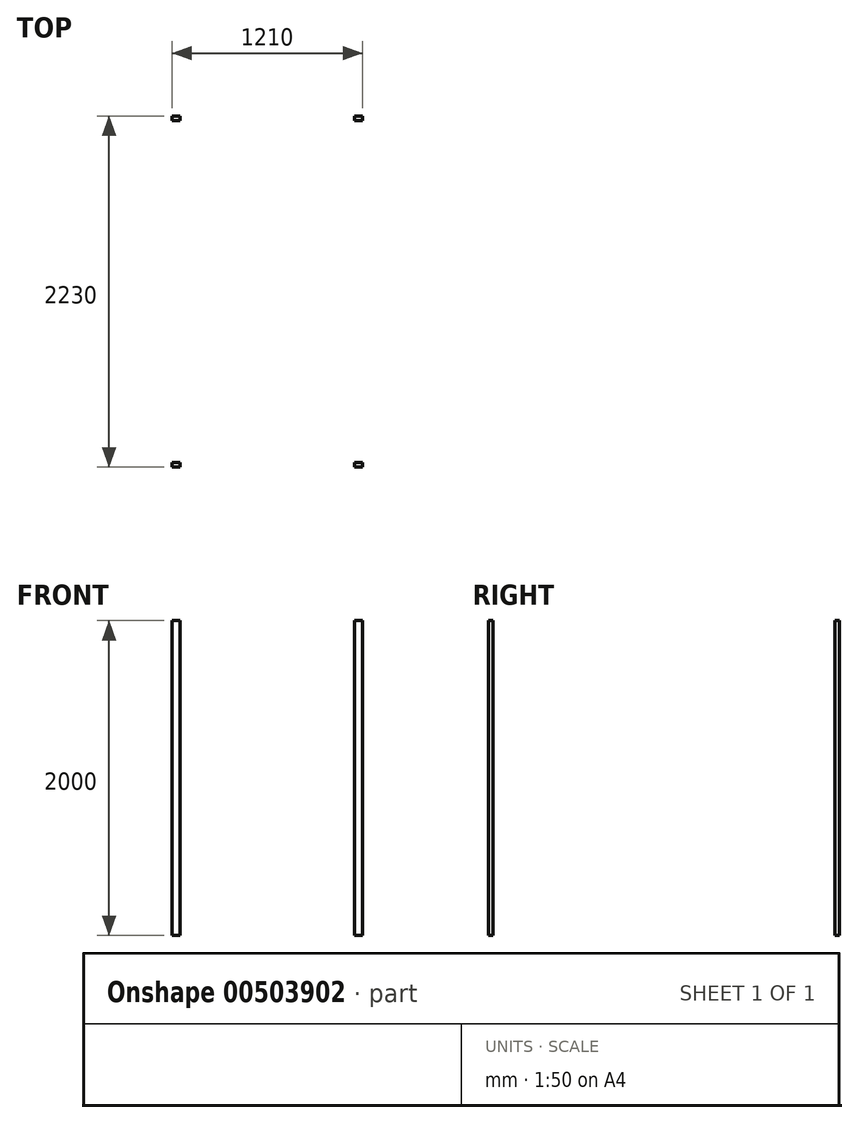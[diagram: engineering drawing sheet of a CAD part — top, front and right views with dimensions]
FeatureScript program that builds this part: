
annotation { "Feature Type Name" : "Feature", "Feature Type Description" : "" }
export const myFeature = defineFeature(function(context is Context, id is Id, definition is map)
    precondition{}
    {
        {
            var Q0;
            Q0=qCreatedBy(makeId("Top.planeOp"),FACE);
            var sketch = newSketch(context, id + "F0", { "sketchPlane" : qUnion([Q0])});
            skLineSegment(sketch, "E0.bottom", {"start": v(-1210, 1130) * mm, "end": v(-1160, 1130) * mm});
            skLineSegment(sketch, "E0.top", {"start": v(-1210, 1100) * mm, "end": v(-1160, 1100) * mm});
            skLineSegment(sketch, "E0.left", {"start": v(-1210, 1130) * mm, "end": v(-1210, 1100) * mm});
            skLineSegment(sketch, "E0.right", {"start": v(-1160, 1130) * mm, "end": v(-1160, 1100) * mm});
            skLineSegment(sketch, "E1.bottom", {"start": v(-50, 1130) * mm, "end": v(0, 1130) * mm});
            skLineSegment(sketch, "E1.top", {"start": v(-50, 1100) * mm, "end": v(0, 1100) * mm});
            skLineSegment(sketch, "E1.left", {"start": v(-50, 1130) * mm, "end": v(-50, 1100) * mm});
            skLineSegment(sketch, "E1.right", {"start": v(0, 1130) * mm, "end": v(0, 1100) * mm});
            skLineSegment(sketch, "E2.bottom", {"start": v(-50, -1070) * mm, "end": v(0, -1070) * mm});
            skLineSegment(sketch, "E2.top", {"start": v(-50, -1100) * mm, "end": v(0, -1100) * mm});
            skLineSegment(sketch, "E2.left", {"start": v(-50, -1070) * mm, "end": v(-50, -1100) * mm});
            skLineSegment(sketch, "E2.right", {"start": v(0, -1070) * mm, "end": v(0, -1100) * mm});
            skLineSegment(sketch, "E3.bottom", {"start": v(-1210, -1070) * mm, "end": v(-1160, -1070) * mm});
            skLineSegment(sketch, "E3.top", {"start": v(-1210, -1100) * mm, "end": v(-1160, -1100) * mm});
            skLineSegment(sketch, "E3.left", {"start": v(-1210, -1070) * mm, "end": v(-1210, -1100) * mm});
            skLineSegment(sketch, "E3.right", {"start": v(-1160, -1070) * mm, "end": v(-1160, -1100) * mm});
            skSolve(sketch);
        }
        {
            var Q0;
            Q0=makeQuery(id+"F0.imprint","IMPRINT",FACE,{"disambiguationData":[TD([[makeQuery(id+"F0.imprint","IMPRINT",EDGE,{"derivedFrom":sQuery(id+"F0.wireOp",EDGE,"E2.bottom")}),-1.0]])]});
            var Q1;
            Q1=makeQuery(id+"F0.imprint","IMPRINT",FACE,{"disambiguationData":[TD([[makeQuery(id+"F0.imprint","IMPRINT",EDGE,{"derivedFrom":sQuery(id+"F0.wireOp",EDGE,"E3.bottom")}),-1.0]])]});
            var Q2;
            Q2=makeQuery(id+"F0.imprint","IMPRINT",FACE,{"disambiguationData":[TD([[makeQuery(id+"F0.imprint","IMPRINT",EDGE,{"derivedFrom":sQuery(id+"F0.wireOp",EDGE,"E1.bottom")}),-1.0]])]});
            var Q3;
            Q3=makeQuery(id+"F0.imprint","IMPRINT",FACE,{"disambiguationData":[TD([[makeQuery(id+"F0.imprint","IMPRINT",EDGE,{"derivedFrom":sQuery(id+"F0.wireOp",EDGE,"E0.bottom")}),-1.0]])]});
            extrude(context, id + "F1", {"entities" : qUnion([Q0, Q1, Q2, Q3]), "depth" : 2000 * mm});
        }
    });
